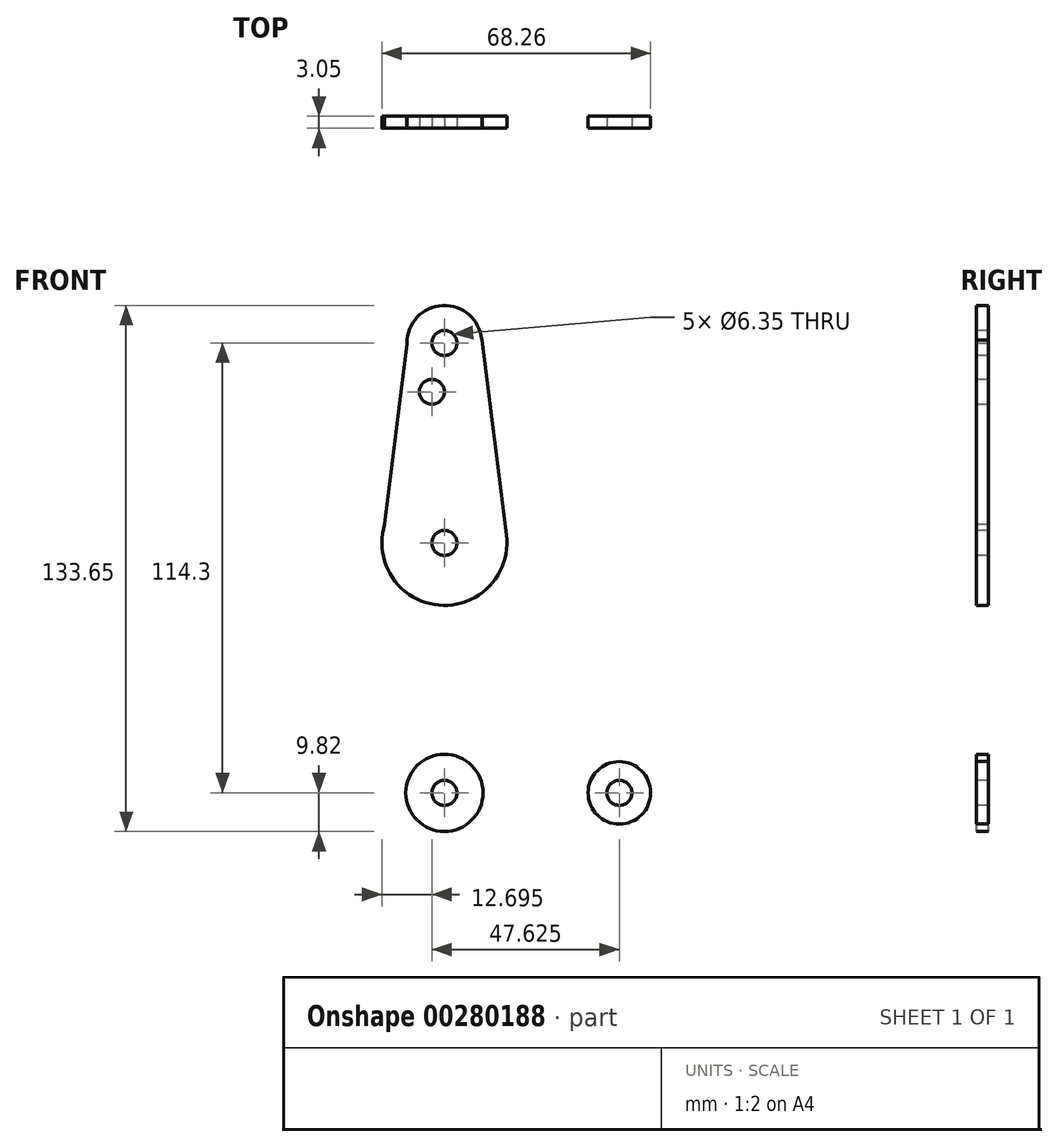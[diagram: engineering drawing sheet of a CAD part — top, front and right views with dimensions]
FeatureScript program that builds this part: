
annotation { "Feature Type Name" : "Feature", "Feature Type Description" : "" }
export const myFeature = defineFeature(function(context is Context, id is Id, definition is map)
    precondition{}
    {
        {
            var Q0;
            Q0=qCreatedBy(makeId("Front.planeOp"),FACE);
            var sketch = newSketch(context, id + "F0", { "sketchPlane" : qUnion([Q0])});
            skLineSegment(sketch, "E0", {"start": v(0, 0) * mm, "end": v(0, 63.5) * mm, "construction": true});
            skCircle(sketch, "E1", {"center": v(0, 63.5) * mm, "radius": 15.88 * mm});
            skLineSegment(sketch, "E2", {"start": v(0, 63.5) * mm, "end": v(0, 114.3) * mm});
            skCircle(sketch, "E3", {"center": v(0, 114.3) * mm, "radius": 9.53 * mm});
            skCircle(sketch, "E4", {"center": v(0, 0) * mm, "radius": 9.82 * mm});
            skLineSegment(sketch, "E5", {"start": v(0, 0) * mm, "end": v(44.45, 0) * mm, "construction": true});
            skCircle(sketch, "E6", {"center": v(44.45, 0) * mm, "radius": 7.94 * mm});
            skLineSegment(sketch, "E7", {"start": v(-9.52, 114.2) * mm, "end": v(-15.85, 62.63) * mm});
            skLineSegment(sketch, "E8", {"start": v(9.5, 115.1) * mm, "end": v(16.11, 62.63) * mm});
            skLineSegment(sketch, "E9", {"start": v(16.11, 62.63) * mm, "end": v(11.62, 17.66) * mm});
            skLineSegment(sketch, "E10", {"start": v(19.23, 8.93) * mm, "end": v(44.76, 7.93) * mm});
            skLineSegment(sketch, "E11", {"start": v(0, -9.82) * mm, "end": v(44.76, -7.93) * mm});
            skCircle(sketch, "E12", {"center": v(0, 114.3) * mm, "radius": 3.18 * mm});
            skCircle(sketch, "E13", {"center": v(0, 63.5) * mm, "radius": 3.18 * mm});
            skCircle(sketch, "E14", {"center": v(0, 0) * mm, "radius": 3.18 * mm});
            skCircle(sketch, "E15", {"center": v(44.45, 0) * mm, "radius": 3.18 * mm});
            skPoint(sketch, "E16.newPointA", {"position": v(9.86, 0) * mm});
            skArc(sketch, "E16.filletArc", {"start": v(11.62, 17.66) * mm, "mid": v(13.54, 11.65) * mm, "end": v(19.23, 8.93) * mm});
            skCircle(sketch, "E17", {"center": v(-3.18, 101.9) * mm, "radius": 3.18 * mm});
            skLineSegment(sketch, "E18", {"start": v(-9.61, 1.99) * mm, "end": v(-15.8, 61.87) * mm});
            skSolve(sketch);
        }
        {
            var Q0;
            Q0 = qSketchRegion(id + "F0", true);
            extrude(context, id + "F1", {"entities" : qUnion([Q0]), "oppositeDirection" : true, "depth" : 3.05 * mm});
        }
    });
